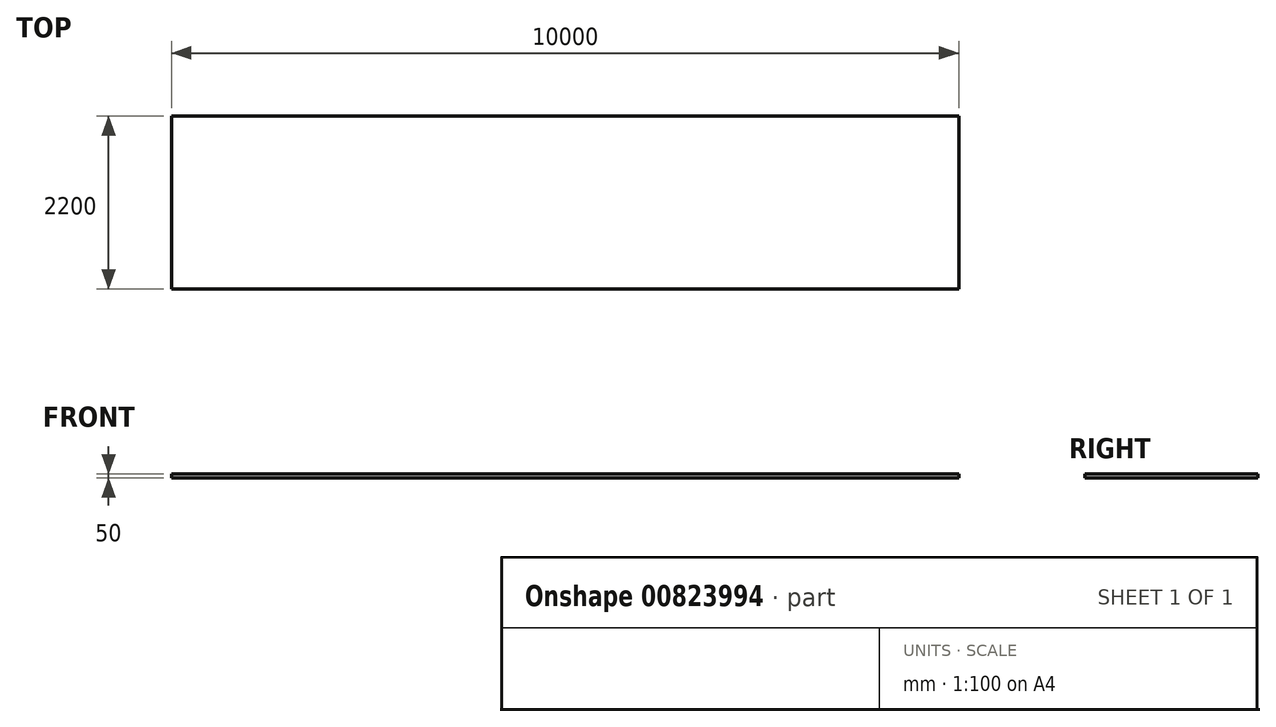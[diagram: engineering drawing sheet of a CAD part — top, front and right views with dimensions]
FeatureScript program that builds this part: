
annotation { "Feature Type Name" : "Feature", "Feature Type Description" : "" }
export const myFeature = defineFeature(function(context is Context, id is Id, definition is map)
    precondition{}
    {
        {
            var Q0;
            Q0=qCreatedBy(makeId("Top.planeOp"),FACE);
            var sketch = newSketch(context, id + "F0", { "sketchPlane" : qUnion([Q0])});
            skLineSegment(sketch, "E0.bottom", {"start": v(-3183.8, 1097.33) * mm, "end": v(6816.2, 1097.33) * mm});
            skLineSegment(sketch, "E0.top", {"start": v(-3183.8, -1102.67) * mm, "end": v(6816.2, -1102.67) * mm});
            skLineSegment(sketch, "E0.left", {"start": v(-3183.8, 1097.33) * mm, "end": v(-3183.8, -1102.67) * mm});
            skLineSegment(sketch, "E0.right", {"start": v(6816.2, 1097.33) * mm, "end": v(6816.2, -1102.67) * mm});
            skSolve(sketch);
        }
        {
            var Q0;
            Q0=makeQuery(id+"F0.imprint","IMPRINT",FACE,{"disambiguationData":[TD([[makeQuery(id+"F0.imprint","IMPRINT",EDGE,{"derivedFrom":sQuery(id+"F0.wireOp",EDGE,"E0.bottom")}),-1.0]])]});
            extrude(context, id + "F1", {"entities" : qUnion([Q0]), "depth" : 50 * mm, "offsetDistance" : 25 * mm});
        }
    });
